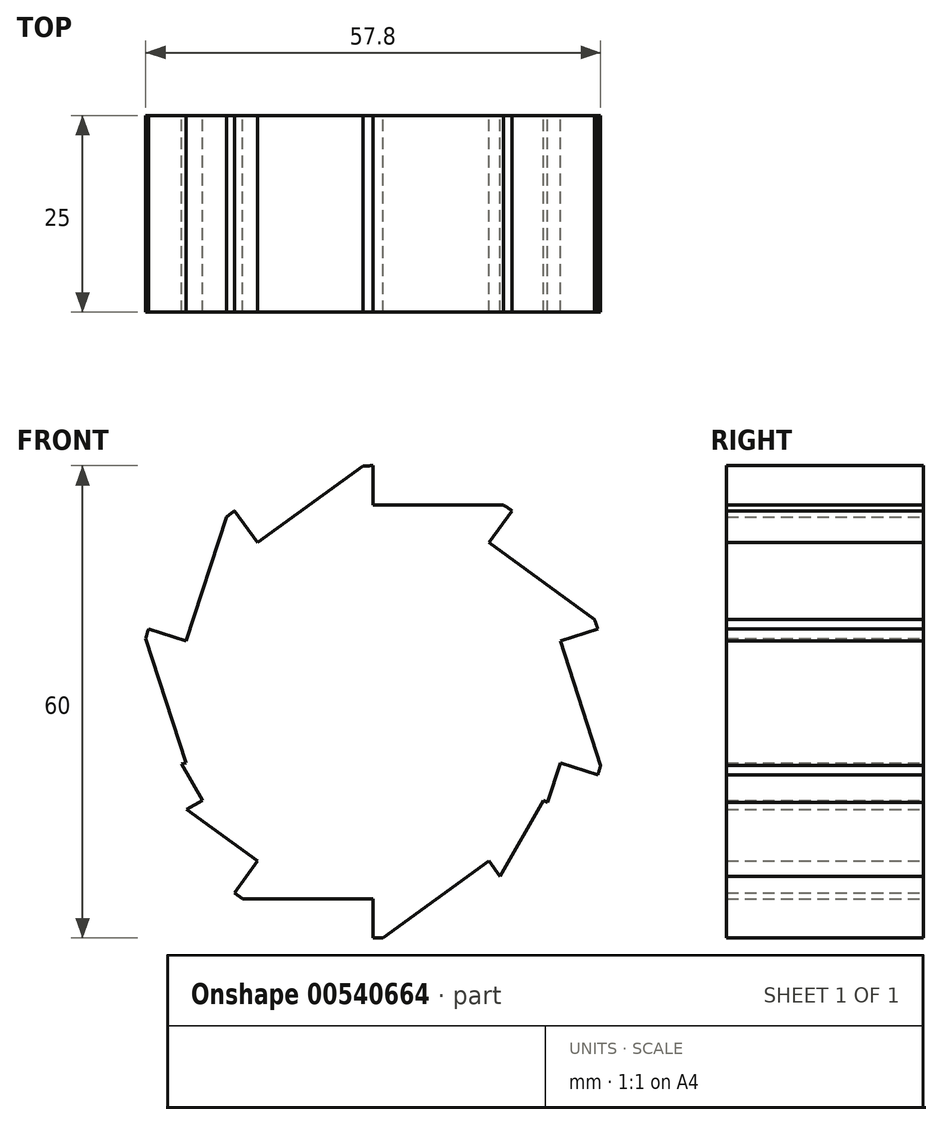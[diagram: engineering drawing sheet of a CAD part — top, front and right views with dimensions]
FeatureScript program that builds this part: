
annotation { "Feature Type Name" : "Feature", "Feature Type Description" : "" }
export const myFeature = defineFeature(function(context is Context, id is Id, definition is map)
    precondition{}
    {
        {
            var Q0;
            Q0=qCreatedBy(makeId("Front.planeOp"),FACE);
            var sketch = newSketch(context, id + "F0", { "sketchPlane" : qUnion([Q0])});
            skCircle(sketch, "E0", {"center": v(0, 0) * mm, "radius": 30 * mm});
            skLineSegment(sketch, "E1", {"start": v(0, 30) * mm, "end": v(0, 25) * mm});
            skLineSegment(sketch, "E2", {"start": v(0, 25) * mm, "end": v(16.58, 25) * mm});
            skLineSegment(sketch, "E3.1.0", {"start": v(-21.65, -12.5) * mm, "end": v(-29.94, 1.86) * mm});
            skLineSegment(sketch, "E3.2.0", {"start": v(21.65, -12.5) * mm, "end": v(13.36, -26.86) * mm});
            skLineSegment(sketch, "E4.1.0", {"start": v(-25.98, -15) * mm, "end": v(-21.65, -12.5) * mm});
            skLineSegment(sketch, "E4.2.0", {"start": v(25.98, -15) * mm, "end": v(21.65, -12.5) * mm});
            skLineSegment(sketch, "E5.1.0", {"start": v(-17.63, 24.27) * mm, "end": v(-14.7, 20.23) * mm});
            skLineSegment(sketch, "E5.1.1", {"start": v(-14.7, 20.23) * mm, "end": v(-1.28, 29.97) * mm});
            skLineSegment(sketch, "E5.2.0", {"start": v(-28.53, 9.27) * mm, "end": v(-23.78, 7.73) * mm});
            skLineSegment(sketch, "E5.2.1", {"start": v(-23.78, 7.73) * mm, "end": v(-18.65, 23.5) * mm});
            skLineSegment(sketch, "E5.3.0", {"start": v(-28.53, -9.27) * mm, "end": v(-23.78, -7.73) * mm});
            skLineSegment(sketch, "E5.3.1", {"start": v(-23.78, -7.73) * mm, "end": v(-28.9, 8.05) * mm});
            skLineSegment(sketch, "E5.4.0", {"start": v(-17.63, -24.27) * mm, "end": v(-14.7, -20.23) * mm});
            skLineSegment(sketch, "E5.4.1", {"start": v(-14.7, -20.23) * mm, "end": v(-28.11, -10.48) * mm});
            skLineSegment(sketch, "E5.5.0", {"start": v(0, -30) * mm, "end": v(0, -25) * mm});
            skLineSegment(sketch, "E5.5.1", {"start": v(0, -25) * mm, "end": v(-16.58, -25) * mm});
            skLineSegment(sketch, "E5.6.0", {"start": v(17.63, -24.27) * mm, "end": v(14.7, -20.23) * mm});
            skLineSegment(sketch, "E5.6.1", {"start": v(14.7, -20.23) * mm, "end": v(1.28, -29.97) * mm});
            skLineSegment(sketch, "E5.7.0", {"start": v(28.53, -9.27) * mm, "end": v(23.78, -7.73) * mm});
            skLineSegment(sketch, "E5.7.1", {"start": v(23.78, -7.73) * mm, "end": v(18.65, -23.5) * mm});
            skLineSegment(sketch, "E5.8.0", {"start": v(28.53, 9.27) * mm, "end": v(23.78, 7.73) * mm});
            skLineSegment(sketch, "E5.8.1", {"start": v(23.78, 7.73) * mm, "end": v(28.9, -8.05) * mm});
            skLineSegment(sketch, "E5.9.0", {"start": v(17.63, 24.27) * mm, "end": v(14.7, 20.23) * mm});
            skLineSegment(sketch, "E5.9.1", {"start": v(14.7, 20.23) * mm, "end": v(28.11, 10.48) * mm});
            skSolve(sketch);
        }
        {
            var Q0;
            {var subQ24=sQuery(id+"F0.wireOp",EDGE,"E1");Q0=makeQuery(id+"F0.imprint","IMPRINT",FACE,{"disambiguationData":[TD([[makeQuery(id+"F0.imprint","IMPRINT",EDGE,{"derivedFrom":subQ24}),-1.0]])]});}
            extrude(context, id + "F1", {"entities" : qUnion([Q0]), "depth" : 25 * mm, "offsetDistance" : 25 * mm});
        }
        {
            var Q0;
            Q0=qCreatedBy(makeId("Front.planeOp"),FACE);
            var sketch = newSketch(context, id + "F2", { "sketchPlane" : qUnion([Q0])});
            skCircle(sketch, "E6", {"center": v(0, 0) * mm, "radius": 8.75 * mm});
            skSolve(sketch);
        }
        {
            var Q0;
            Q0 = qSketchRegion(id + "F2", true);
            extrude(context, id + "F3", {"entities" : qUnion([Q0]), "operationType" : NewBodyOperationType.ADD, "depth" : 25 * mm, "offsetDistance" : 25 * mm});
        }
    });
